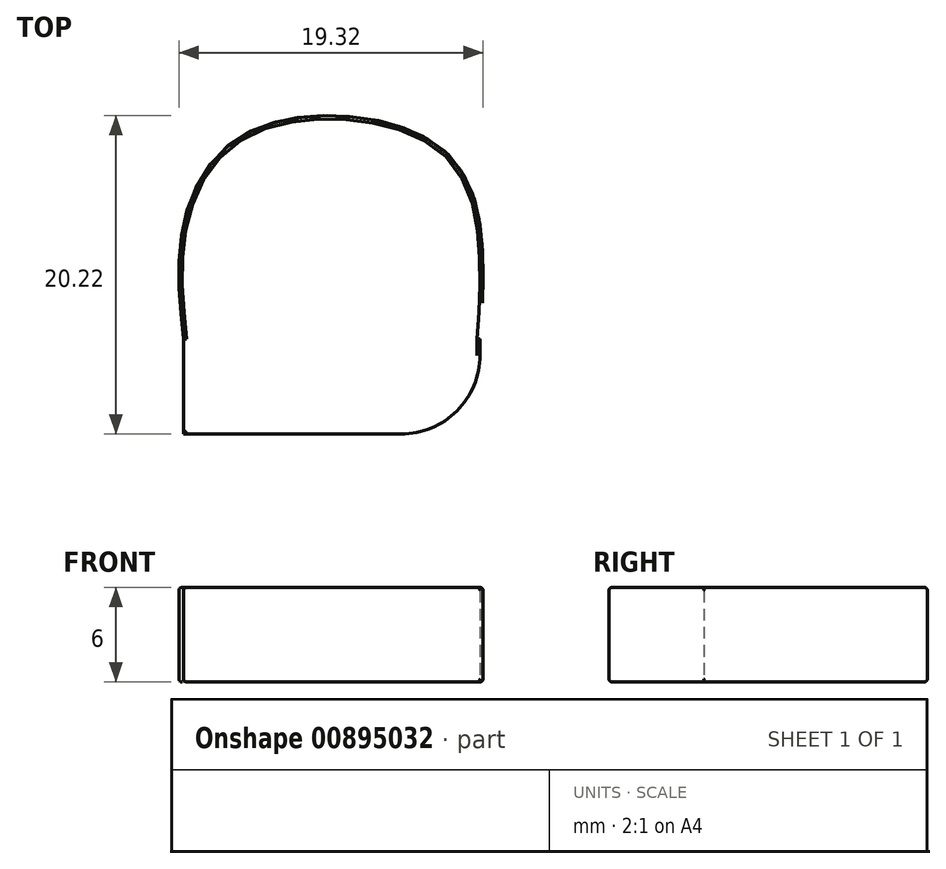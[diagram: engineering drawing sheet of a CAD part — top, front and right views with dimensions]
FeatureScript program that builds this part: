
annotation { "Feature Type Name" : "Feature", "Feature Type Description" : "" }
export const myFeature = defineFeature(function(context is Context, id is Id, definition is map)
    precondition{}
    {
        {
            var Q0;
            Q0=qCreatedBy(makeId("Top.planeOp"),FACE);
            var sketch = newSketch(context, id + "F0", { "sketchPlane" : qUnion([Q0])});
            skFitSpline(sketch, "E0", {"points": [v(9.41, 3.57) * mm, v(9.41, -3.7) * mm, v(5.2, -9.6) * mm, v(-5.2, -9.6) * mm, v(-9.41, -3.7) * mm, v(-9.41, 3.57) * mm, v(-9.41, 3.57) * mm, v(-9.41, 3.57) * mm, v(-9.41, 5.08) * mm, v(-9.41, 6.59) * mm]});
            skFitSpline(sketch, "E1", {"points": [v(-9.41, 6.59) * mm, v(-9.41, 8.04) * mm, v(-9.41, 9.52) * mm, v(-9.41, 9.6) * mm, v(-9.41, 9.6) * mm, v(-9.41, 9.6) * mm]});
            skFitSpline(sketch, "E2", {"points": [v(-9.41, 9.6) * mm, v(-9.41, 9.6) * mm, v(-9.41, 9.6) * mm, v(-9.17, 9.6) * mm, v(9.17, 9.6) * mm, v(9.41, 9.6) * mm, v(9.41, 9.6) * mm, v(9.41, 9.6) * mm]});
            skFitSpline(sketch, "E3", {"points": [v(9.41, 9.6) * mm, v(9.41, 9.6) * mm, v(9.41, 9.6) * mm, v(9.41, 9.44) * mm, v(9.41, 3.73) * mm, v(9.41, 3.57) * mm, v(9.41, 3.57) * mm, v(9.41, 3.57) * mm]});
            skSolve(sketch);
        }
        {
            var Q0;
            Q0=makeQuery(id+"F0.imprint","IMPRINT",FACE,{"disambiguationData":[TD([[makeQuery(id+"F0.imprint","IMPRINT",EDGE,{"derivedFrom":sQuery(id+"F0.wireOp",EDGE,"E0")}),-1.0]])]});
            extrude(context, id + "F1", {"entities" : qUnion([Q0]), "depth" : 6 * mm, "offsetDistance" : 25 * mm});
        }
        {
            var Q0;
            Q0=makeQuery(id+"F1.opExtrude","SWEPT_BODY",BODY,{"disambiguationData":[OSD([sQuery(id+"F0.wireOp",EDGE,"E0"),sQuery(id+"F0.wireOp",EDGE,"E1"),sQuery(id+"F0.wireOp",EDGE,"E2"),sQuery(id+"F0.wireOp",EDGE,"E3")])]});
            var Q1;
            Q1=makeQuery(id+"F1.opExtrude","SWEPT_EDGE",EDGE,{"disambiguationData":[OSD([sQuery(id+"F0.wireOp",EDGE,"E2"),sQuery(id+"F0.wireOp",EDGE,"E3")])]});
            transform(context, id + "F2", {"entities" : qUnion([Q0]), "transformType" : TransformType.ROTATION, "transformAxis" : qUnion([Q1]), "angle" : 180 * degree, "makeCopy" : false});
        }
        {
            var Q0;
            Q0=makeQuery(id+"F1.opExtrude","CAP_FACE",FACE,{"disambiguationData":[OSD([sQuery(id+"F0.wireOp",EDGE,"E0"),sQuery(id+"F0.wireOp",EDGE,"E1"),sQuery(id+"F0.wireOp",EDGE,"E2"),sQuery(id+"F0.wireOp",EDGE,"E3")])],"isStart":false});
            var Q1;
            Q1=makeQuery(id+"F1.opExtrude","CAP_FACE",FACE,{"disambiguationData":[OSD([sQuery(id+"F0.wireOp",EDGE,"E0"),sQuery(id+"F0.wireOp",EDGE,"E1"),sQuery(id+"F0.wireOp",EDGE,"E2"),sQuery(id+"F0.wireOp",EDGE,"E3")])],"isStart":true});
            fillet(context, id + "F3", {"entities" : qUnion([Q0, Q1]), "radius" : 0.2 * mm, "tangentPropagation" : true, "allowEdgeOverflow" : false});
        }
        {
            var Q0;
            Q0=makeQuery(id+"F1.opExtrude","SWEPT_EDGE",EDGE,{"disambiguationData":[OSD([sQuery(id+"F0.wireOp",EDGE,"E1"),sQuery(id+"F0.wireOp",EDGE,"E2")])]});
            fillet(context, id + "F4", {"entities" : qUnion([Q0]), "radius" : 5 * mm, "tangentPropagation" : true, "allowEdgeOverflow" : false});
        }
    });
